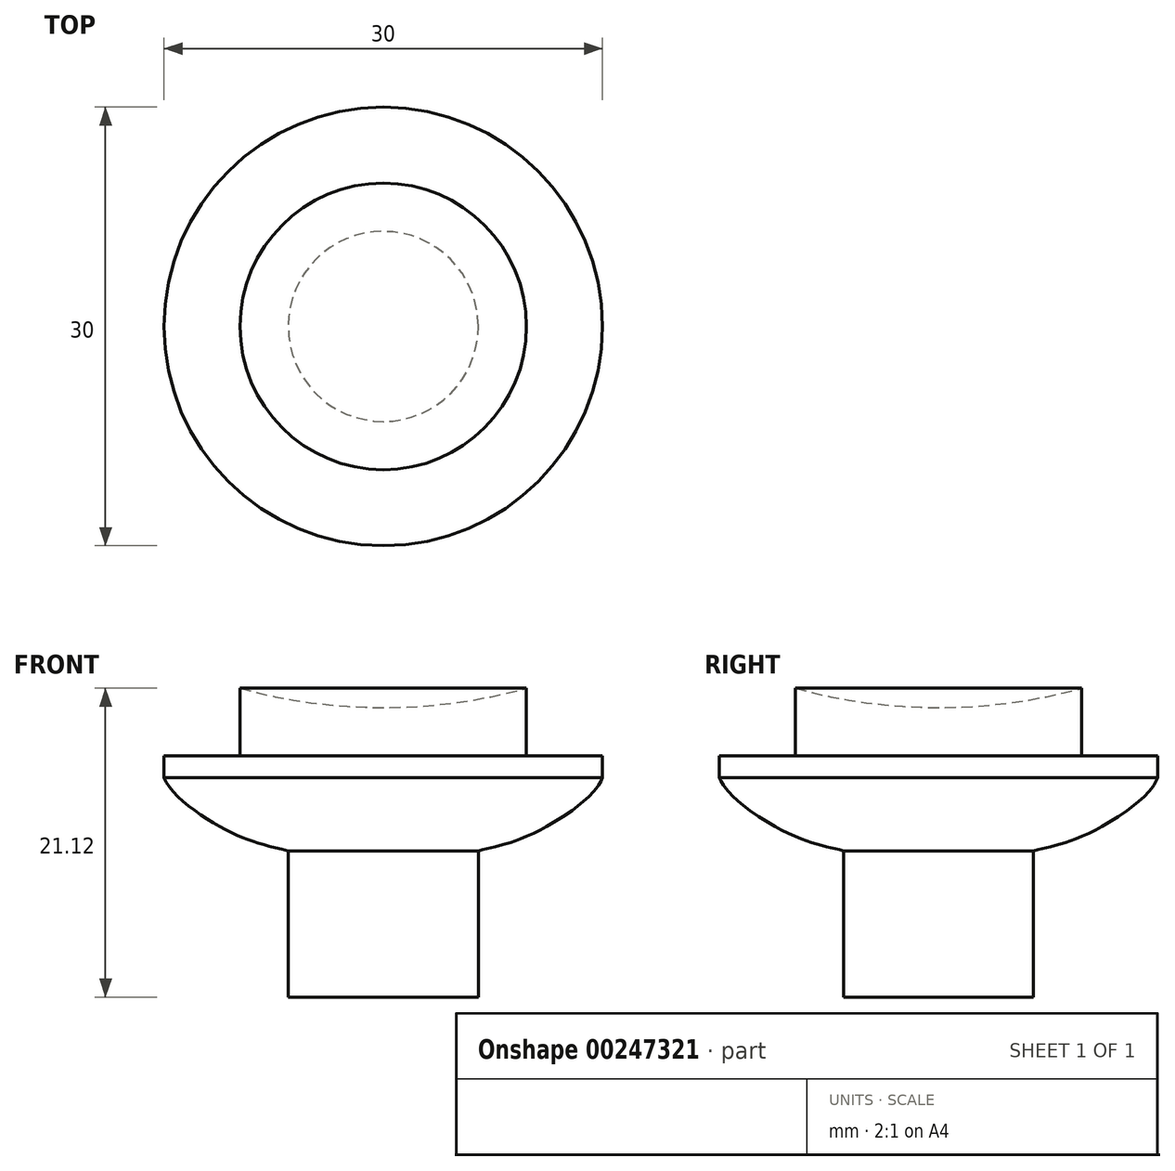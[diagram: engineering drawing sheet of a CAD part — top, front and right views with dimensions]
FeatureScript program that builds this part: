
annotation { "Feature Type Name" : "Feature", "Feature Type Description" : "" }
export const myFeature = defineFeature(function(context is Context, id is Id, definition is map)
    precondition{}
    {
        {
            var Q0;
            Q0=qCreatedBy(makeId("Top.planeOp"),FACE);
            var sketch = newSketch(context, id + "F0", { "sketchPlane" : qUnion([Q0])});
            skArc(sketch, "E0", {"start": v(0, -37) * mm, "mid": v(37, 0) * mm, "end": v(0, 37) * mm});
            skLineSegment(sketch, "E1", {"start": v(0, 38.44) * mm, "end": v(0, -38.44) * mm});
            skSolve(sketch);
        }
        {
            var Q0;
            {var subQ0=sQuery(id+"F0.wireOp",EDGE,"DYxJ9GRZ-q8qz-Q0Qq-K3Mr-sF3iiEksJAOO");Q0=makeQuery(id+"F0.imprint","IMPRINT",FACE,{"disambiguationData":[TD([[makeQuery(id+"F0.imprint","IMPRINT",EDGE,{"derivedFrom":subQ0}),1.0]])]});}
            var Q1;
            {var subQ0=sQuery(id+"F0.wireOp",EDGE,"E0");Q1=makeQuery(id+"F0.imprint","IMPRINT",FACE,{"disambiguationData":[TD([[makeQuery(id+"F0.imprint","IMPRINT",EDGE,{"derivedFrom":subQ0}),1.0]])]});}
            var Q2;
            Q2=sQuery(id+"F0.wireOp",EDGE,"E1");
            revolve(context, id + "F1", {"entities" : qUnion([Q0, Q1]), "axis" : qUnion([Q2]), "revolveType" : RevolveType.FULL});
        }
        {
            var Q0;
            Q0=qCreatedBy(makeId("Top.planeOp"),FACE);
            cPlane(context, id + "F2", {"entities" : qUnion([Q0]), "cplaneType" : CPlaneType.OFFSET, "offset" : 40 * mm, "width" : 150 * mm, "height" : 150 * mm});
        }
        {
            var Q0;
            Q0=qCreatedBy(id+"F2.planeOp",FACE);
            var sketch = newSketch(context, id + "F3", { "sketchPlane" : qUnion([Q0])});
            skCircle(sketch, "E2", {"center": v(0, 0) * mm, "radius": 9.8 * mm});
            skSolve(sketch);
        }
        {
            var Q0;
            Q0=makeQuery(id+"F3.imprint","IMPRINT",FACE,{"disambiguationData":[TD([[makeQuery(id+"F3.imprint","IMPRINT",EDGE,{"derivedFrom":sQuery(id+"F3.wireOp",EDGE,"E2")}),1.0]])]});
            extrude(context, id + "F4", {"entities" : qUnion([Q0]), "oppositeDirection" : true, "depth" : 10 * mm, "hasSecondDirection" : true, "secondDirectionOppositeDirection" : false, "secondDirectionDepth" : 0.3 * mm});
        }
        {
            var Q0;
            Q0=makeQuery(id+"F1.opRevolve","SWEPT_BODY",BODY,{"disambiguationData":[OSD([sQuery(id+"F0.wireOp",EDGE,"E0"),sQuery(id+"F0.wireOp",EDGE,"E1")])]});
            var Q1;
            Q1=makeQuery(id+"F4.opExtrude","SWEPT_BODY",BODY,{"disambiguationData":[OSD([sQuery(id+"F3.wireOp",EDGE,"E2")])]});
            booleanBodies(context, id + "F5", {"operationType" : BooleanOperationType.SUBTRACTION, "tools" : qUnion([Q0]), "targets" : qUnion([Q1])});
        }
        {
            var Q0;
            Q0=makeQuery(id+"F4.opExtrude","CAP_FACE",FACE,{"disambiguationData":[OSD([sQuery(id+"F3.wireOp",EDGE,"E2")])],"isStart":true});
            var sketch = newSketch(context, id + "F6", { "sketchPlane" : qUnion([Q0])});
            skPoint(sketch, "E3.0", {"position": v(0, 0) * mm});
            skLineSegment(sketch, "E4.bottom", {"start": v(25, -25) * mm, "end": v(-25, -25) * mm});
            skLineSegment(sketch, "E4.top", {"start": v(25, 25) * mm, "end": v(-25, 25) * mm});
            skLineSegment(sketch, "E4.left", {"start": v(25, -25) * mm, "end": v(25, 25) * mm});
            skLineSegment(sketch, "E4.right", {"start": v(-25, -25) * mm, "end": v(-25, 25) * mm});
            skCircle(sketch, "E5", {"center": v(0, 0) * mm, "radius": 15 * mm});
            skSolve(sketch);
        }
        {
            var Q0;
            Q0=makeQuery(id+"F6.imprint","IMPRINT",FACE,{"disambiguationData":[TD([[makeQuery(id+"F6.imprint","IMPRINT",EDGE,{"derivedFrom":makeQuery(id+"F4.opExtrude","CAP_EDGE",EDGE,{"disambiguationData":[OSD([sQuery(id+"F3.wireOp",EDGE,"E2")])],"isStart":true})}),1.0]])]});
            var Q1;
            Q1=makeQuery(id+"F6.imprint","IMPRINT",FACE,{"disambiguationData":[TD([[makeQuery(id+"F6.imprint","IMPRINT",EDGE,{"derivedFrom":sQuery(id+"F6.wireOp",EDGE,"E5")}),1.0]])]});
            extrude(context, id + "F7", {"entities" : qUnion([Q0, Q1]), "operationType" : NewBodyOperationType.ADD, "depth" : 1.5 * mm});
        }
        {
            var Q0;
            Q0=makeQuery(id+"F7.opExtrude","CAP_FACE",FACE,{"disambiguationData":[OSD([sQuery(id+"F6.wireOp",EDGE,"E5")])],"isStart":false});
            var sketch = newSketch(context, id + "F8", { "sketchPlane" : qUnion([Q0])});
            skLineSegment(sketch, "E6", {"start": v(-25, 25) * mm, "end": v(25, -25) * mm});
            skLineSegment(sketch, "E7", {"start": v(25, -25) * mm, "end": v(25, 25) * mm});
            skLineSegment(sketch, "E8", {"start": v(25, 25) * mm, "end": v(-25, -25) * mm});
            skLineSegment(sketch, "E9", {"start": v(-25, -25) * mm, "end": v(-25, 25) * mm});
            skLineSegment(sketch, "E10", {"start": v(0, -25) * mm, "end": v(0, 25) * mm});
            skSolve(sketch);
        }
        {
            var Q0;
            Q0=makeQuery(id+"F4.opExtrude","SWEPT_BODY",BODY,{"disambiguationData":[OSD([sQuery(id+"F3.wireOp",EDGE,"E2")])]});
            var Q1;
            Q1=sQuery(id+"F8.wireOp",EDGE,"E10");
            transform(context, id + "F9", {"entities" : qUnion([Q0]), "transformType" : TransformType.ROTATION, "transformAxis" : qUnion([Q1]), "angle" : 180 * degree, "makeCopy" : false});
        }
        {
            var Q0;
            Q0=makeQuery(id+"F7.opExtrude","CAP_FACE",FACE,{"disambiguationData":[OSD([sQuery(id+"F6.wireOp",EDGE,"E5")])],"isStart":false});
            var sketch = newSketch(context, id + "F10", { "sketchPlane" : qUnion([Q0])});
            skCircle(sketch, "E11", {"center": v(0, 0) * mm, "radius": 6.5 * mm});
            skSolve(sketch);
        }
        {
            var Q0;
            Q0=makeQuery(id+"F10.imprint","IMPRINT",FACE,{"disambiguationData":[TD([[makeQuery(id+"F10.imprint","IMPRINT",EDGE,{"derivedFrom":sQuery(id+"F10.wireOp",EDGE,"E11")}),1.0]])]});
            extrude(context, id + "F11", {"entities" : qUnion([Q0]), "operationType" : NewBodyOperationType.ADD, "depth" : 15 * mm});
        }
        {
            var Q0;
            Q0=qCreatedBy(makeId("Front.planeOp"),FACE);
            var sketch = newSketch(context, id + "F12", { "sketchPlane" : qUnion([Q0])});
            skLineSegment(sketch, "E12.0", {"start": v(15, 41.8) * mm, "end": v(-15, 41.8) * mm});
            skLineSegment(sketch, "E13", {"start": v(6.5, 41.8) * mm, "end": v(6.5, 26.8) * mm});
            skLineSegment(sketch, "E14", {"start": v(-6.5, 26.8) * mm, "end": v(-6.5, 41.8) * mm});
            skLineSegment(sketch, "E15", {"start": v(6.5, 36.8) * mm, "end": v(-6.5, 36.8) * mm, "construction": true});
            skPoint(sketch, "E16.1.internal.snap0", {"position": v(-10.75, 39.3) * mm});
            skFitSpline(sketch, "E16", {"points": [v(-15, 41.8) * mm, v(-10.75, 38.24) * mm, v(-6.5, 36.8) * mm], "startDerivative": vector(2.7, -7.18) * mm, "endDerivative": vector(10.94, -2.56) * mm});
            skFitSpline(sketch, "E17.MirrorCS", {"points": [v(15, 41.8) * mm, v(10.75, 38.24) * mm, v(6.5, 36.8) * mm], "startDerivative": vector(-2.7, -7.18) * mm, "endDerivative": vector(-10.94, -2.56) * mm});
            skSolve(sketch);
        }
        {
            var Q0;
            Q0=qCreatedBy(makeId("Front.planeOp"),FACE);
            var sketch = newSketch(context, id + "F13", { "sketchPlane" : qUnion([Q0])});
            skLineSegment(sketch, "E18", {"start": v(0, 29.77) * mm, "end": v(0, 45.24) * mm});
            skSolve(sketch);
        }
        {
            var Q0;
            {var subQ0=sQuery(id+"F12.wireOp",EDGE,"E16");Q0=makeQuery(id+"F12.imprint","IMPRINT",FACE,{"disambiguationData":[TD([[makeQuery(id+"F12.imprint","IMPRINT",EDGE,{"derivedFrom":subQ0}),1.0]])]});}
            var Q1;
            Q1=sQuery(id+"F13.wireOp",EDGE,"E18");
            revolve(context, id + "F14", {"operationType" : NewBodyOperationType.ADD, "entities" : qUnion([Q0]), "axis" : qUnion([Q1]), "revolveType" : RevolveType.FULL});
        }
    });
